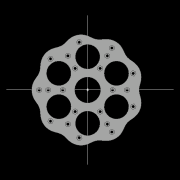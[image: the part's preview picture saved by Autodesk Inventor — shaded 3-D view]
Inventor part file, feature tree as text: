
AUTODESK INVENTOR PART (.ipt)
format: ipt  version: 2022.2 (Build 262287010, 287A)  size: 822,784 bytes
history: native  units: mm
features: other x20, extrude x17, sketch x12, pattern_circular x7, plane x4, fillet x2, move_body x2, revolve x2, draft x2, chamfer x2
ambient origin geometry x8: Origin, YZ Plane, XZ Plane, XY Plane, X Axis, Y Axis, Z Axis, Center Point
bodies: Solid5 (feature_tree)
feature tree (70):
  other  "CrossSection1"
  sketch  "Sketch7"  dims[d90=15.767323mm]
  other  "Roller1"
  other  "Roller2"
  sketch  "Sketch22"  dims[d167=8.972256mm]
  sketch  "Sketch2"  dims[d57=4.025mm]
  sketch  "Sketch23"  dims[d173=10.814812mm]
  other  "RevRoller1"
  fillet  "Fillet1"  Radius=13.336791mm
  pattern_circular  "Circular Pattern13"  Count=360  [1 undecoded]
  move_body  "Move Body7"
  revolve  "Revolution13"  [1 undecoded]
  fillet  "Fillet3"  Radius=0.025mm
  pattern_circular  "Circular Pattern14"  [2 undecoded]
  move_body  "Move Body6"
  revolve  "Revolution14"  [1 undecoded]
  other  "OuterRim_Top2"
  other  "OuterRim_Bottom2"
  extrude  "Rotor_Ring"  Depth=0.25mm
  draft  "FaceDraft2"
  sketch  "Sketch30"  dims[d201=53.5mm d232=0.0mm d233=3600.0mm]
  plane  "Work Plane5"
  other  "Rotor Featurs"
  other  "RotorRim_Bottom"
  extrude  "Extrusion24"  Depth=0.25mm
  extrude  "Extrusion25"  Depth=1.0mm
  extrude  "Extrusion26"  TaperAngle=90.0deg  [1 undecoded]
  pattern_circular  "Circular Pattern23"  [2 undecoded]
  sketch  "Sketch41"  dims[d346=0.025mm]
  extrude  "Extrusion27"  Depth=0.25mm
  extrude  "Extrusion28"  TaperAngle=360.0deg  [1 undecoded]
  pattern_circular  "Circular Pattern24"  Angle=30.0deg  [1 undecoded]
  extrude  "Extrusion29"  Depth=0.25mm
  extrude  "Extrusion30"  Depth=0.25mm
  extrude  "Extrusion31"  Depth=0.25mm
  pattern_circular  "Circular Pattern25"  [2 undecoded]
  sketch  "Sketch42"  dims[d347=0.1mm]
  extrude  "Extrusion32"  TaperAngle=30.0deg  [1 undecoded]
  extrude  "Extrusion33"  TaperAngle=90.0deg  [1 undecoded]
  extrude  "Extrusion34"  Depth=0.25mm
  extrude  "Extrusion35"  Depth=0.25mm
  pattern_circular  "Circular Pattern26"  Angle=360.0deg  [1 undecoded]
  pattern_circular  "Circular Pattern27"  Angle=90.0deg  [1 undecoded]
  chamfer  "Chamfer1"  Distance=0.1mm
  chamfer  "Chamfer2"  Distance=0.025mm
  draft  "FaceDraft4"
  plane  "Work Plane7"
  sketch  "Sketch44"  dims[d349=17.374602mm]
  sketch  "Sketch45"  dims[d350=17.374329mm]
  extrude  "Extrusion39"  Depth=0.25mm
  extrude  "Extrusion40"  Depth=0.25mm
  plane  "Work Plane8"
  sketch  "Sketch46"  dims[d351=0.025mm d352=0.025mm d354=0.025mm d355=17.374329mm d356=17.374602mm d357=1.0mm d358=90.0deg d359=0.5mm d360=60.0mm d361=360.0deg d363=30.0deg d367=8.1mm d369=4.014775mm d370=0.025mm d371=1.0mm d372=30.0deg d373=90.0deg d374=0.5mm d375=60.0mm d376=360.0deg d378=90.0deg d379=0.1mm d380=0.025mm d381=0.025mm d382=0.025mm d383=0.025mm d384=10.461905mm d385=0.0mm d386=0.0mm d391=1.0mm d392=53.5mm d393=1.5mm d394=1.5mm d395=1.5mm d396=1.5mm d397=90.0deg d398=90.0deg d399=90.0deg d400=53.5mm d401=10.461905mm d402=0.0mm d486=0.436332mm d487=0.5mm d488=2.0mm d489=0.0mm d490=20.0mm d495=2.5mm d496=8.0mm d506=13.856406mm d507=55.5mm d508=8.0mm d509=0.05mm d510=2.5mm d511=30.0deg d512=12.0mm d513=6.0mm d514=0.2mm d515=30.0deg d516=131.0mm d517=65.5mm d518=0.2mm d519=100.0mm d520=120.0mm d521=2.0mm d522=150.0mm d530=50.0mm d531=5.5mm d532=5.5mm d533=5.5mm d534=87.0mm d535=73.5mm d536=55.0mm d537=27.0mm d538=3.0mm d539=2.4mm d540=0.0mm d541=0.0mm d542=0.0mm d543=5.5mm d544=3.0mm d545=0.0mm d546=90.0mm d547=360.0deg d549=3.0mm d550=3.0mm d551=2.4mm d552=0.0mm d553=5.230953mm d554=0.0mm d555=2.4mm d556=0.0mm d557=5.230953mm d558=0.0mm d559=5.230953mm d560=0.0mm d561=90.0mm d562=360.0deg d564=60.0mm d565=360.0deg d567=5.5mm d568=5.5mm d569=3.0mm d570=0.0mm d571=5.230953mm d572=0.0mm d573=3.0mm d574=0.0mm d575=5.230953mm d576=0.0mm d577=90.0mm d578=360.0deg d580=60.0mm d581=360.0deg d584=20.0mm d585=8.0mm d587=1.75mm d589=3.0mm d592=2.0mm d593=12.0mm d594=12.0mm d600=0.5mm d601=2.0mm d602=45.0deg d603=0.5mm d604=2.0mm d605=45.0deg d606=0.436332mm d607=0.5mm d608=0.0mm d609=20.0mm d611=360.0deg d613=0.0mm d614=0.0mm d615=50.0mm d617=1.0mm d618=3.0mm d619=20.0mm d621=360.0deg d623=0.8mm d624=0.0mm d625=0.8mm d626=0.0mm d627=20.0mm d635=12.0mm d640=2.5mm d641=100.0mm d643=360.0deg d645=0.0mm d646=3600.0mm d16=0.872665mm d17=0.872665mm d49=0.872665mm d50=0.872665mm d51=0.872665mm d52=0.872665mm d236=0.5mm d237=0.872665mm d238=0.5mm d239=0.872665mm d282=1.0mm d283=1.0mm d284=1.0mm d285=0.15mm d286=0.25mm d287=0.375mm d288=14.3117mm d289=0.75mm d290=20.594885mm d291=0.0625mm d292=0.75mm d293=0.375mm d405=0.5mm d406=0.872665mm d407=0.5mm d408=0.872665mm d413=0.5mm d414=0.872665mm d415=0.5mm d416=0.872665mm d417=0.5mm d418=0.872665mm d419=0.5mm d420=0.872665mm d421=0.872665mm d431=0.5mm d432=0.872665mm d433=0.5mm d434=0.872665mm d471=0.5mm d472=0.872665mm d473=0.5mm d474=0.872665mm d497=0.5mm d498=0.872665mm d499=0.5mm d500=0.872665mm d590=0.5mm d591=0.872665mm]
  plane  "Work Plane6"
  sketch  "Sketch43"  dims[d348=0.1mm]
  extrude  "Extrusion37"  Depth=0.25mm
  extrude  "Extrusion38"  Depth=10.461905mm
  other  "2D Equation Curve1"
  sketch  "Sketch40"  dims[d343=17.374329mm d344=17.374602mm d345=0.025mm]
  other  "Work Axis6"
  other  "Work Axis7"
  other  "Work Axis8"
  other  "Work Axis9"
  other  "Work Axis10"
  other  "Work Point1"
  other  "Work Point2"
  other  "Work Point3"
  other  "Work Point4"
  other  "Work Point5"
  other  "2D Equation Curve2"
note: 16 required parameter values undecoded (feature->parameter linkage not recoverable at this tier; creation-order binding heuristic only, values carry confidence <= 0.55)